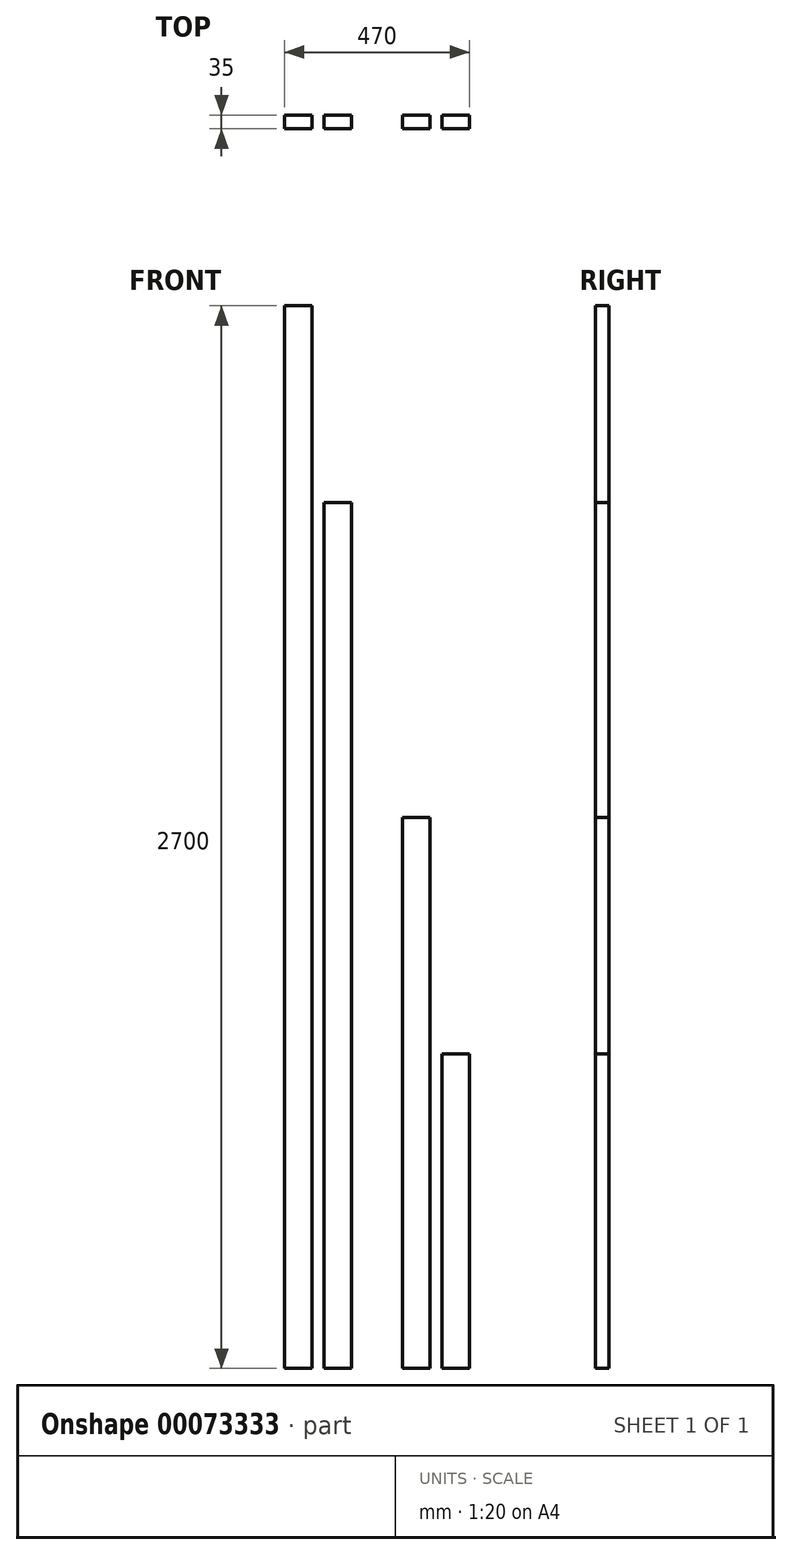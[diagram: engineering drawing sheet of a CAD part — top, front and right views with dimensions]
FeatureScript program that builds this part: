
annotation { "Feature Type Name" : "Feature", "Feature Type Description" : "" }
export const myFeature = defineFeature(function(context is Context, id is Id, definition is map)
    precondition{}
    {
        {
            var Q0;
            Q0=qCreatedBy(makeId("Top.planeOp"),FACE);
            var sketch = newSketch(context, id + "F0", { "sketchPlane" : qUnion([Q0])});
            skLineSegment(sketch, "E0.bottom", {"start": v(0, 0) * mm, "end": v(70, 0) * mm});
            skLineSegment(sketch, "E0.top", {"start": v(0, 35) * mm, "end": v(70, 35) * mm});
            skLineSegment(sketch, "E0.left", {"start": v(0, 0) * mm, "end": v(0, 35) * mm});
            skLineSegment(sketch, "E0.right", {"start": v(70, 0) * mm, "end": v(70, 35) * mm});
            skLineSegment(sketch, "E1.1.0.0", {"start": v(100, 0) * mm, "end": v(100, 35) * mm});
            skLineSegment(sketch, "E1.1.0.1", {"start": v(100, 35) * mm, "end": v(170, 35) * mm});
            skLineSegment(sketch, "E1.1.0.2", {"start": v(100, 0) * mm, "end": v(170, 0) * mm});
            skLineSegment(sketch, "E1.1.0.3", {"start": v(170, 0) * mm, "end": v(170, 35) * mm});
            skLineSegment(sketch, "E1.2.0.0", {"start": v(200, 0) * mm, "end": v(200, 35) * mm});
            skLineSegment(sketch, "E1.2.0.1", {"start": v(200, 35) * mm, "end": v(270, 35) * mm});
            skLineSegment(sketch, "E1.2.0.2", {"start": v(200, 0) * mm, "end": v(270, 0) * mm});
            skLineSegment(sketch, "E1.2.0.3", {"start": v(270, 0) * mm, "end": v(270, 35) * mm});
            skLineSegment(sketch, "E1.3.0.0", {"start": v(300, 0) * mm, "end": v(300, 35) * mm});
            skLineSegment(sketch, "E1.3.0.1", {"start": v(300, 35) * mm, "end": v(370, 35) * mm});
            skLineSegment(sketch, "E1.3.0.2", {"start": v(300, 0) * mm, "end": v(370, 0) * mm});
            skLineSegment(sketch, "E1.3.0.3", {"start": v(370, 0) * mm, "end": v(370, 35) * mm});
            skLineSegment(sketch, "E1.4.0.0", {"start": v(400, 0) * mm, "end": v(400, 35) * mm});
            skLineSegment(sketch, "E1.4.0.1", {"start": v(400, 35) * mm, "end": v(470, 35) * mm});
            skLineSegment(sketch, "E1.4.0.2", {"start": v(400, 0) * mm, "end": v(470, 0) * mm});
            skLineSegment(sketch, "E1.4.0.3", {"start": v(470, 0) * mm, "end": v(470, 35) * mm});
            skLineSegment(sketch, "E1.5.0.0", {"start": v(500, 0) * mm, "end": v(500, 35) * mm});
            skLineSegment(sketch, "E1.5.0.1", {"start": v(500, 35) * mm, "end": v(570, 35) * mm});
            skLineSegment(sketch, "E1.5.0.2", {"start": v(500, 0) * mm, "end": v(570, 0) * mm});
            skLineSegment(sketch, "E1.5.0.3", {"start": v(570, 0) * mm, "end": v(570, 35) * mm});
            skLineSegment(sketch, "E1.direction1", {"start": v(0, 0) * mm, "end": v(100, 0) * mm, "construction": true});
            skSolve(sketch);
        }
        {
            var Q0;
            Q0=makeQuery(id+"F0.imprint","IMPRINT",FACE,{"disambiguationData":[TD([[makeQuery(id+"F0.imprint","IMPRINT",EDGE,{"derivedFrom":sQuery(id+"F0.wireOp",EDGE,"E0.bottom")}),1.0]])]});
            extrude(context, id + "F1", {"entities" : qUnion([Q0]), "depth" : 2700 * mm});
        }
        {
            var Q0;
            Q0=makeQuery(id+"F0.imprint","IMPRINT",FACE,{"disambiguationData":[TD([[makeQuery(id+"F0.imprint","IMPRINT",EDGE,{"derivedFrom":sQuery(id+"F0.wireOp",EDGE,"E1.1.0.0")}),-1.0]])]});
            extrude(context, id + "F2", {"entities" : qUnion([Q0]), "depth" : 2200 * mm});
        }
        {
            var Q0;
            Q0=makeQuery(id+"F0.imprint","IMPRINT",FACE,{"disambiguationData":[TD([[makeQuery(id+"F0.imprint","IMPRINT",EDGE,{"derivedFrom":sQuery(id+"F0.wireOp",EDGE,"E1.3.0.0")}),-1.0]])]});
            extrude(context, id + "F3", {"entities" : qUnion([Q0]), "depth" : 1400 * mm});
        }
        {
            var Q0;
            Q0=makeQuery(id+"F0.imprint","IMPRINT",FACE,{"disambiguationData":[TD([[makeQuery(id+"F0.imprint","IMPRINT",EDGE,{"derivedFrom":sQuery(id+"F0.wireOp",EDGE,"E1.4.0.0")}),-1.0]])]});
            extrude(context, id + "F4", {"entities" : qUnion([Q0]), "depth" : 800 * mm});
        }
    });
